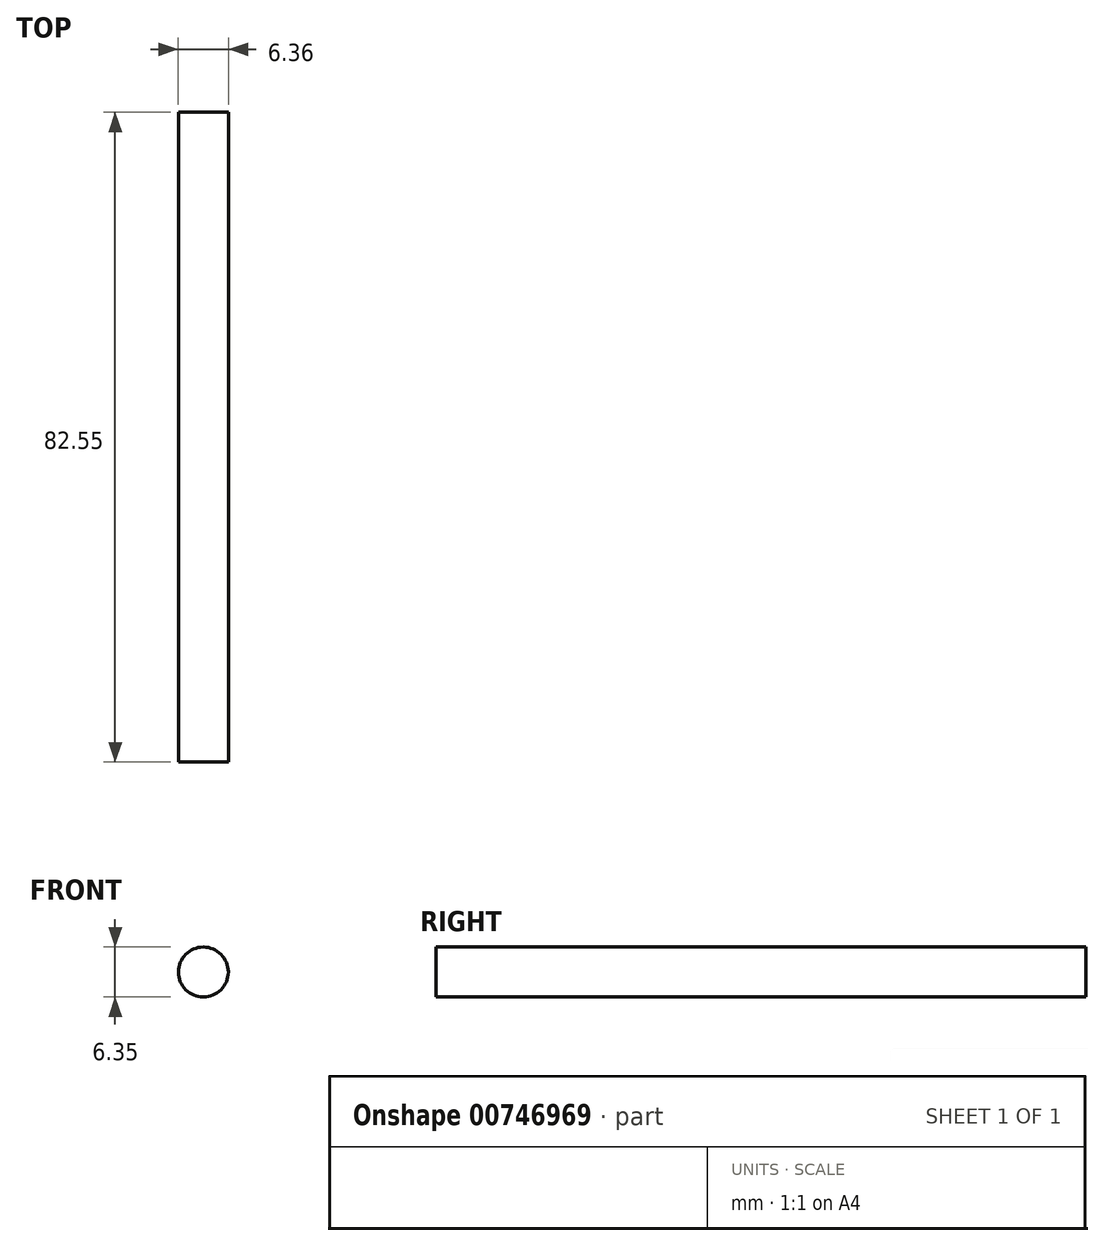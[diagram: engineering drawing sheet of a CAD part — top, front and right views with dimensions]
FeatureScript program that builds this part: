
annotation { "Feature Type Name" : "Feature", "Feature Type Description" : "" }
export const myFeature = defineFeature(function(context is Context, id is Id, definition is map)
    precondition{}
    {
        {
            var Q0;
            Q0=qCreatedBy(makeId("Right.planeOp"),FACE);
            var sketch = newSketch(context, id + "F0", { "sketchPlane" : qUnion([Q0])});
            skLineSegment(sketch, "E0.bottom", {"start": v(-28.56, -0.87) * mm, "end": v(54, -0.87) * mm});
            skLineSegment(sketch, "E0.top", {"start": v(-28.56, 5.48) * mm, "end": v(54, 5.48) * mm});
            skLineSegment(sketch, "E0.left", {"start": v(-28.56, -0.87) * mm, "end": v(-28.56, 5.48) * mm});
            skLineSegment(sketch, "E0.right", {"start": v(54, -0.87) * mm, "end": v(54, 5.48) * mm});
            skLineSegment(sketch, "E1", {"start": v(54, 2.3) * mm, "end": v(-35.6, 2.3) * mm});
            skSolve(sketch);
        }
        {
            var Q0;
            {var subQ0=sQuery(id+"F0.wireOp",EDGE,"E0.bottom");Q0=makeQuery(id+"F0.imprint","IMPRINT",FACE,{"disambiguationData":[TD([[makeQuery(id+"F0.imprint","IMPRINT",EDGE,{"derivedFrom":subQ0}),1.0]])]});}
            var Q1;
            Q1=sQuery(id+"F0.wireOp",EDGE,"E1");
            revolve(context, id + "F1", {"surfaceOperationType" : NewSurfaceOperationType.NEW, "entities" : qUnion([Q0]), "axis" : qUnion([Q1]), "revolveType" : RevolveType.FULL});
        }
    });
